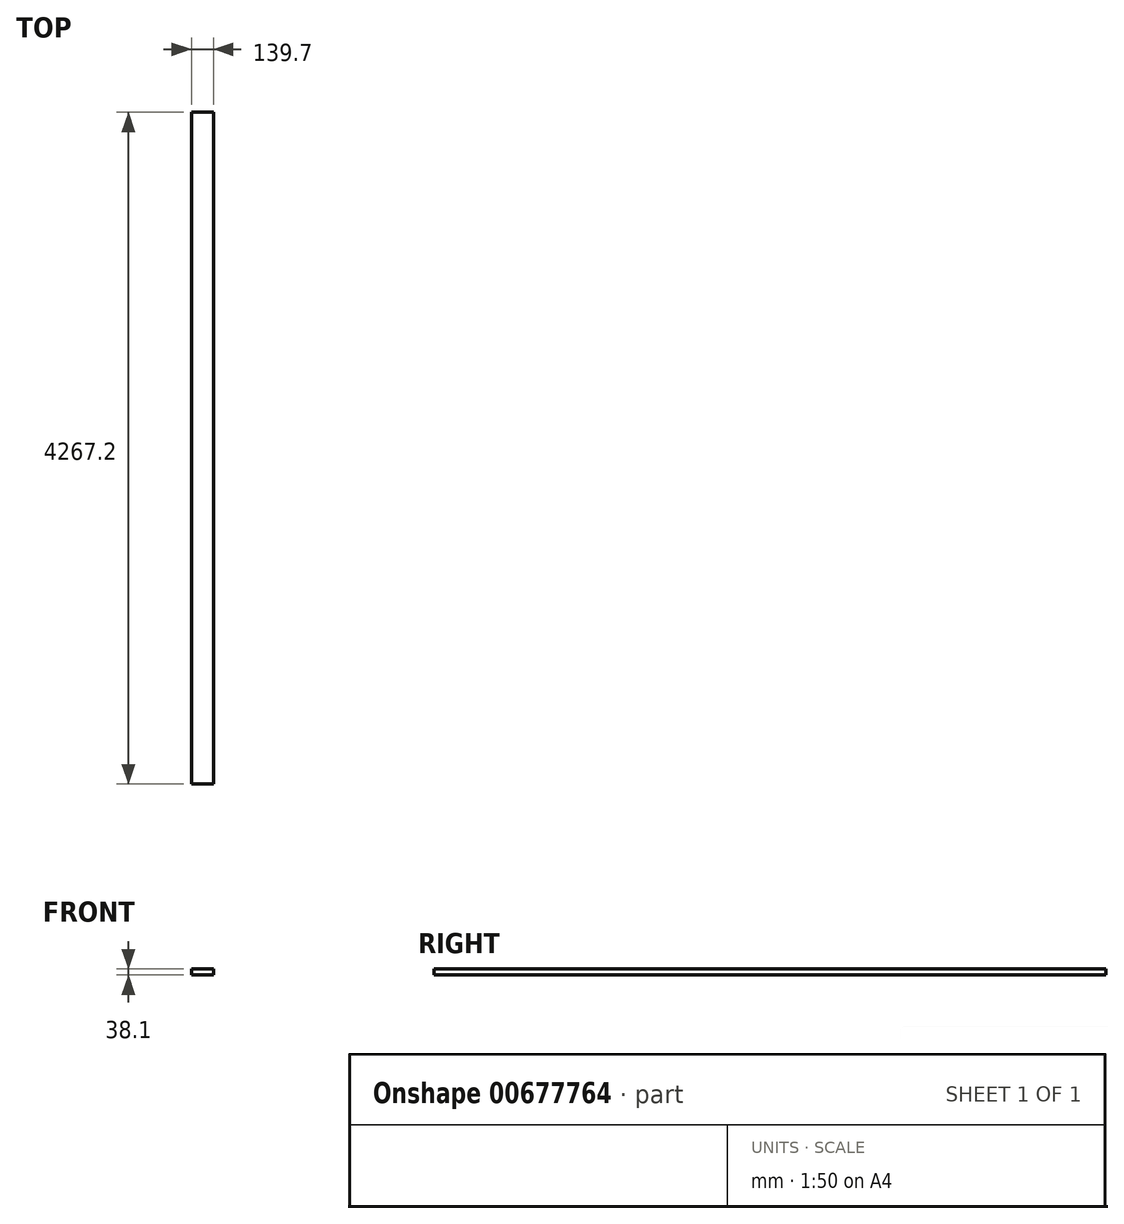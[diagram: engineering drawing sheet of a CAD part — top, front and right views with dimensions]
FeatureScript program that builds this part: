
annotation { "Feature Type Name" : "Feature", "Feature Type Description" : "" }
export const myFeature = defineFeature(function(context is Context, id is Id, definition is map)
    precondition{}
    {
        {
            var Q0;
            Q0=qCreatedBy(makeId("Front.planeOp"),FACE);
            var sketch = newSketch(context, id + "F0", { "sketchPlane" : qUnion([Q0])});
            skLineSegment(sketch, "E0.bottom", {"start": v(-451.99, -107.42) * mm, "end": v(-591.69, -107.42) * mm});
            skLineSegment(sketch, "E0.top", {"start": v(-451.99, -69.32) * mm, "end": v(-591.69, -69.32) * mm});
            skLineSegment(sketch, "E0.left", {"start": v(-451.99, -107.42) * mm, "end": v(-451.99, -69.32) * mm});
            skLineSegment(sketch, "E0.right", {"start": v(-591.69, -107.42) * mm, "end": v(-591.69, -69.32) * mm});
            skSolve(sketch);
        }
        {
            var Q0;
            Q0=makeQuery(id+"F0.imprint","IMPRINT",FACE,{"disambiguationData":[TD([[makeQuery(id+"F0.imprint","IMPRINT",EDGE,{"derivedFrom":sQuery(id+"F0.wireOp",EDGE,"E0.bottom")}),-1.0]])]});
            extrude(context, id + "F1", {"entities" : qUnion([Q0]), "depth" : 4267.2 * mm, "offsetDistance" : 25.4 * mm});
        }
    });
